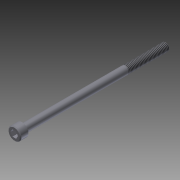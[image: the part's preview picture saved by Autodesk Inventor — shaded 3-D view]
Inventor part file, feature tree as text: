
AUTODESK INVENTOR PART (.ipt)
format: ipt  version: 2011 (Build 150239000, 239)  size: 93,184 bytes
history: native  units: in
note: dims shown in document units (in); Inventor stores cm internally (conversion verified against a paired STEP export)
features: extrude x3, sketch x3, chamfer x2, thread x1
ambient origin geometry x8: Origin, YZ Plane, XZ Plane, XY Plane, X Axis, Y Axis, Z Axis, Center Point
bodies: Solid1 (feature_tree)
feature tree (9):
  extrude  "Extrusion1"  Depth=0.19in TaperAngle=0.0deg
  extrude  "Extrusion2"  Depth=3.5in TaperAngle=0.0deg
  extrude  "Extrusion3"  Depth=0.125in TaperAngle=0.0deg
  thread  "Thread1"  [1 undecoded]
  chamfer  "Chamfer1"  Distance=0.02in Angle=45.0deg
  chamfer  "Chamfer2"  Distance=0.02in Angle=45.0deg
  sketch  "Sketch1"  dims[d0=0.312in d1=0.19in d2=0.0in]
  sketch  "Sketch2"  dims[d3=0.19in d4=3.5in d5=0.0in]
  sketch  "Sketch3"  dims[d6=0.1562in d7=0.125in d8=0.0in d9=1.0in d10=0.0in d11=0.02in d12=0.125in d13=45.0deg d14=0.02in d15=0.125in d16=45.0deg]
note: 1 required parameter value undecoded (feature->parameter linkage not recoverable at this tier; creation-order binding heuristic only, values carry confidence <= 0.55)
